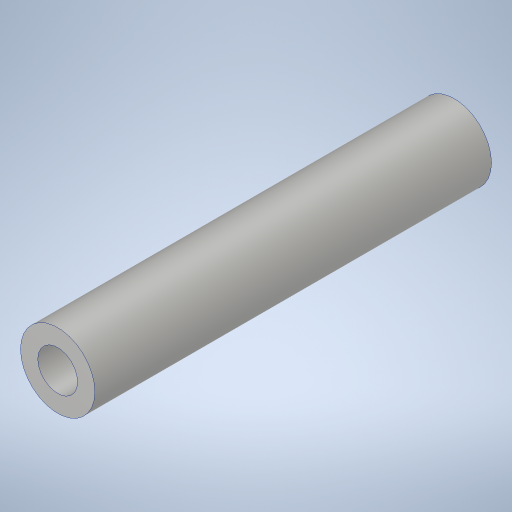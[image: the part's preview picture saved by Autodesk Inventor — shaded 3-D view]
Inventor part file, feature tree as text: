
AUTODESK INVENTOR PART (.ipt)
format: ipt  version: 2023.4 (Build 274418000, 418)  size: 237,056 bytes
history: native  units: in
note: dims shown in document units (in); Inventor stores cm internally (conversion verified against a paired STEP export)
features: extrude x1, hole x1
ambient origin geometry x8: Origin, YZ Plane, XZ Plane, XY Plane, X Axis, Y Axis, Z Axis, Center Point
bodies: Solid1 (feature_tree)
feature tree (2):
  extrude  "Extrusion1"  Depth=2.0in
  hole  "Hole1"  [1 undecoded]
note: 1 required parameter value undecoded (feature->parameter linkage not recoverable at this tier; creation-order binding heuristic only, values carry confidence <= 0.55)
